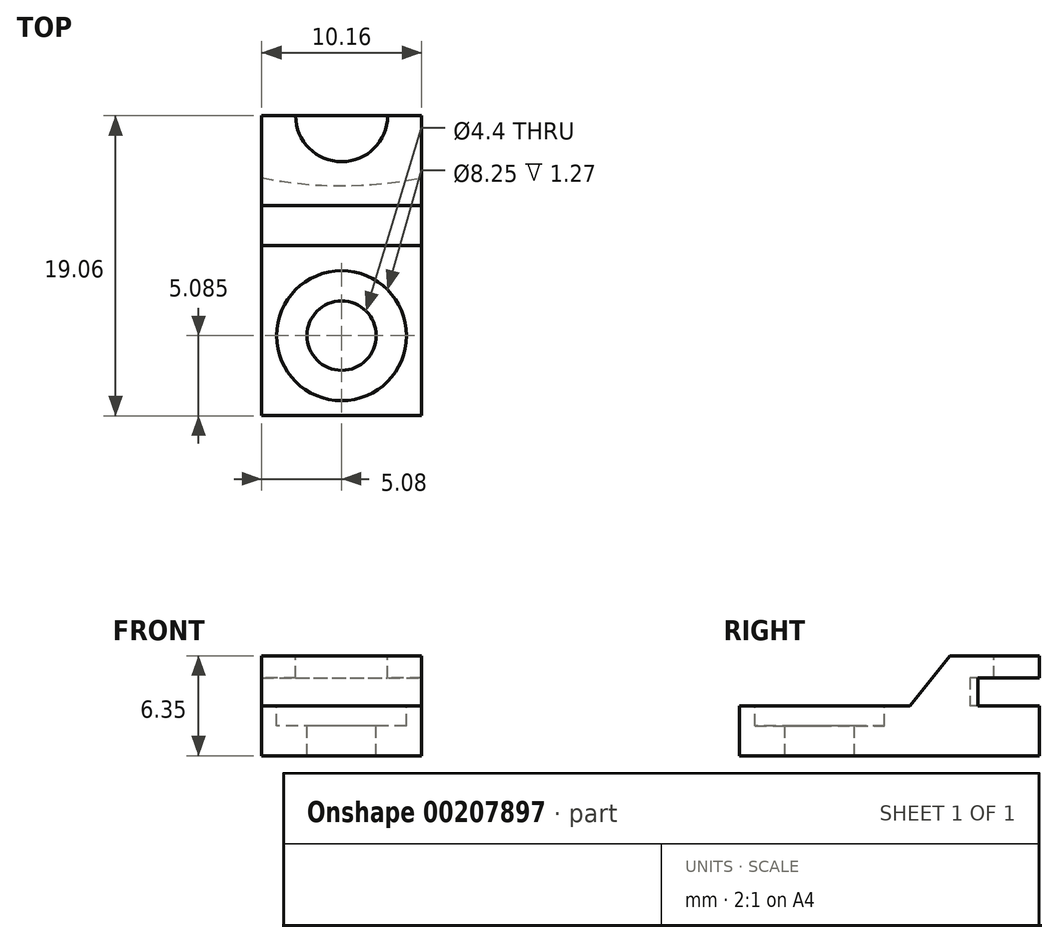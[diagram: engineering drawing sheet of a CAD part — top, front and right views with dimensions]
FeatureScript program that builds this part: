
annotation { "Feature Type Name" : "Feature", "Feature Type Description" : "" }
export const myFeature = defineFeature(function(context is Context, id is Id, definition is map)
    precondition{}
    {
        {
            var Q0;
            Q0=qCreatedBy(makeId("Top.planeOp"),FACE);
            var sketch = newSketch(context, id + "F0", { "sketchPlane" : qUnion([Q0])});
            skLineSegment(sketch, "E0.bottom", {"start": v(5.08, -9.53) * mm, "end": v(-5.08, -9.53) * mm});
            skLineSegment(sketch, "E0.top", {"start": v(5.08, 9.53) * mm, "end": v(-5.08, 9.53) * mm});
            skLineSegment(sketch, "E0.left", {"start": v(5.08, -9.52) * mm, "end": v(5.08, 9.53) * mm});
            skLineSegment(sketch, "E0.right", {"start": v(-5.08, -9.53) * mm, "end": v(-5.08, 9.52) * mm});
            skPoint(sketch, "E0.middle", {"position": v(0, 0) * mm});
            skSolve(sketch);
        }
        {
            var Q0;
            Q0=qSketchRegion(id+"F0",true);
            extrude(context, id + "F1", {"entities" : qUnion([Q0]), "depth" : 3.17 * mm});
        }
        {
            var Q0;
            Q0=makeQuery(id+"F1.opExtrude","SWEPT_FACE",FACE,{"disambiguationData":[OSD([sQuery(id+"F0.wireOp",EDGE,"E0.left")])]});
            var sketch = newSketch(context, id + "F2", { "sketchPlane" : qUnion([Q0])});
            skLineSegment(sketch, "E1", {"start": v(1.27, 3.18) * mm, "end": v(3.81, 6.35) * mm});
            skLineSegment(sketch, "E2", {"start": v(3.81, 6.35) * mm, "end": v(9.53, 6.35) * mm});
            skLineSegment(sketch, "E3", {"start": v(9.53, 6.35) * mm, "end": v(9.53, 3.18) * mm});
            skLineSegment(sketch, "E4", {"start": v(9.53, 3.17) * mm, "end": v(1.27, 3.17) * mm});
            skSolve(sketch);
        }
        {
            var Q0;
            Q0=makeQuery(id+"F2.imprint","IMPRINT",FACE,{"disambiguationData":[TD([[makeQuery(id+"F2.imprint","IMPRINT",EDGE,{"derivedFrom":sQuery(id+"F2.wireOp",EDGE,"E1")}),-1.0]])]});
            var sketch = newSketch(context, id + "F3", { "sketchPlane" : qUnion([Q0])});
            skSolve(sketch);
        }
        {
            var Q0;
            Q0=makeQuery(id+"F2.imprint","IMPRINT",FACE,{"disambiguationData":[TD([[makeQuery(id+"F2.imprint","IMPRINT",EDGE,{"derivedFrom":sQuery(id+"F2.wireOp",EDGE,"E1")}),-1.0]])]});
            var Q1;
            Q1=makeQuery(id+"F1.opExtrude","SWEPT_FACE",FACE,{"disambiguationData":[OSD([sQuery(id+"F0.wireOp",EDGE,"E0.right")])]});
            extrude(context, id + "F4", {"entities" : qUnion([Q0]), "operationType" : NewBodyOperationType.ADD, "endBound" : BoundingType.UP_TO_SURFACE, "oppositeDirection" : true, "endBoundEntityFace" : qUnion([Q1]), "depth" : 25.4 * mm});
        }
        {
            var Q0;
            Q0=makeQuery(id+"F1.opExtrude","CAP_FACE",FACE,{"disambiguationData":[OSD([sQuery(id+"F0.wireOp",EDGE,"E0.bottom"),sQuery(id+"F0.wireOp",EDGE,"E0.top"),sQuery(id+"F0.wireOp",EDGE,"E0.left"),sQuery(id+"F0.wireOp",EDGE,"E0.right")])],"isStart":false});
            var sketch = newSketch(context, id + "F5", { "sketchPlane" : qUnion([Q0])});
            skPoint(sketch, "E5", {"position": v(0, -4.45) * mm});
            skSolve(sketch);
        }
        {
            var Q0;
            Q0=sQuery(id+"F5.wireOp",VERTEX,"E5");
            var Q1;
            Q1=makeQuery(id+"F1.opExtrude","SWEPT_BODY",BODY,{"disambiguationData":[OSD([sQuery(id+"F0.wireOp",EDGE,"E0.bottom"),sQuery(id+"F0.wireOp",EDGE,"E0.top"),sQuery(id+"F0.wireOp",EDGE,"E0.left"),sQuery(id+"F0.wireOp",EDGE,"E0.right")])]});
            hole(context, id + "F6", {"style" : HoleStyle.C_BORE, "endStyle" : HoleEndStyle.BLIND, "holeDiameter" : 4.4 * mm, "cBoreDiameter" : 8.25 * mm, "cBoreDepth" : 1.27 * mm, "holeDepth" : 12.7 * mm, "startFromSketch" : true, "locations" : qUnion([Q0]), "scope" : qUnion([Q1])});
        }
        {
            var Q0;
            Q0=makeQuery(id+"F1.opExtrude","CAP_FACE",FACE,{"disambiguationData":[OSD([sQuery(id+"F0.wireOp",EDGE,"E0.bottom"),sQuery(id+"F0.wireOp",EDGE,"E0.top"),sQuery(id+"F0.wireOp",EDGE,"E0.left"),sQuery(id+"F0.wireOp",EDGE,"E0.right")])],"isStart":false});
            var sketch = newSketch(context, id + "F7", { "sketchPlane" : qUnion([Q0])});
            skCircle(sketch, "E6", {"center": v(0, 30.48) * mm, "radius": 25.4 * mm});
            skSolve(sketch);
        }
        {
            var Q0;
            Q0=makeQuery(id+"F7.imprint","IMPRINT",FACE,{"disambiguationData":[TD([[makeQuery(id+"F7.imprint","IMPRINT",EDGE,{"derivedFrom":sQuery(id+"F7.wireOp",EDGE,"E6")}),1.0]])]});
            extrude(context, id + "F8", {"entities" : qUnion([Q0]), "operationType" : NewBodyOperationType.REMOVE, "depth" : 1.78 * mm});
        }
        {
            var Q0;
            Q0=makeQuery(id+"F4.opExtrude","SWEPT_FACE",FACE,{"disambiguationData":[OSD([sQuery(id+"F2.wireOp",EDGE,"E2")])]});
            var sketch = newSketch(context, id + "F9", { "sketchPlane" : qUnion([Q0])});
            skCircle(sketch, "E7", {"center": v(0, 9.53) * mm, "radius": 2.92 * mm});
            skPoint(sketch, "E7.centerSnap0", {"position": v(0, 9.53) * mm});
            skSolve(sketch);
        }
        {
            var Q0;
            Q0 = qSketchRegion(id + "F9", true);
            extrude(context, id + "F10", {"entities" : qUnion([Q0]), "operationType" : NewBodyOperationType.REMOVE, "oppositeDirection" : true, "depth" : 2.54 * mm});
        }
    });
